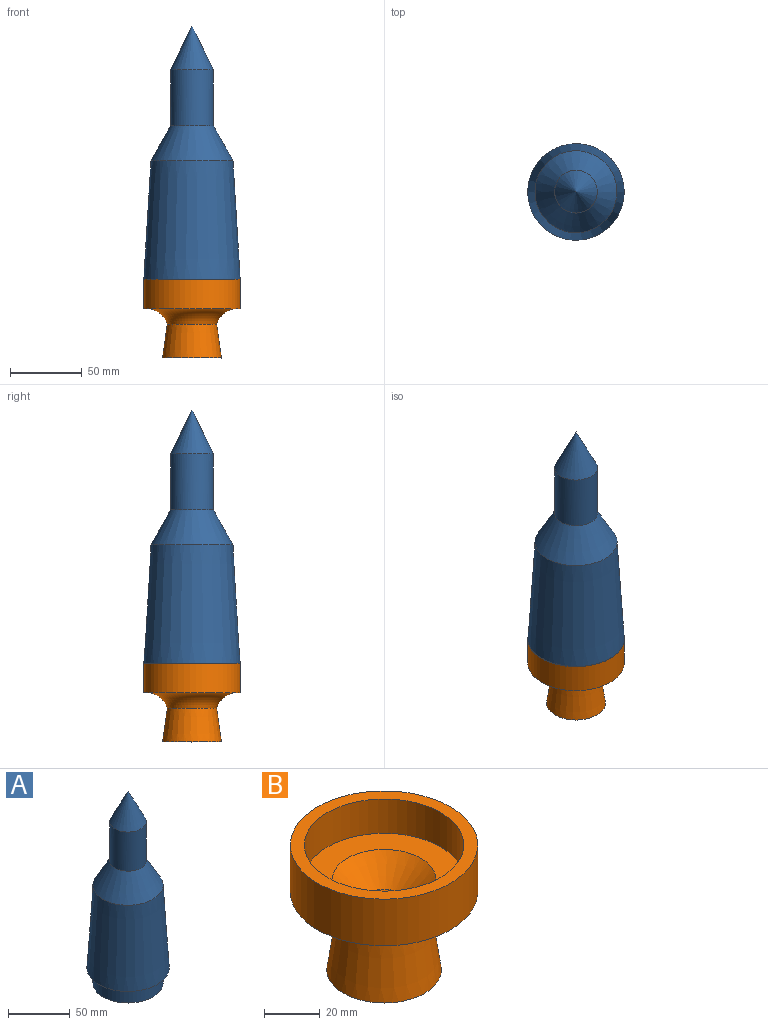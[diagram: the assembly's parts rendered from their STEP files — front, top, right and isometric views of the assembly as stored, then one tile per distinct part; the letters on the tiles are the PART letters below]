
ASSEMBLY  parts=2 mates=1
PART A: 13 faces, bbox 67x67x191 mm
  f0: cylinder r=28.5mm len=57mm, axis (0,0,1), area 2686.1mm2, adj f1,f12
  f1: plane 57x57mm, normal (0,0,-1), area 1476.5mm2, adj f0,f2
  f2: cone r=18.5mm half-angle=14.6deg, axis (0,0,1), area 3375.5mm2, adj f1,f3
  f3: cylinder r=24.75mm len=53.85mm, axis (0,0,1), area 8372.8mm2, adj f2,f4
  f4: revolved ~49.49x49.49mm, area 3906.6mm2, adj f3,f5
  f5: cone r=10.07mm half-angle=36.8deg, axis (0,0,1), area 430.9mm2, adj f4,f6
  f6: cylinder r=10.07mm len=46.25mm, axis (0,0,1), area 2925.6mm2, adj f5,f7
  f7: plane 20.13x20.13mm, normal (0,0,-1), area 318.4mm2, adj f6
  f8: cone r=14.84mm half-angle=26deg, axis (0,0,-1), area 1578.3mm2, adj f9
  f9: cylinder r=14.84mm len=38.88mm, axis (0,0,1), area 3626.4mm2, adj f8,f10
  f10: cone r=28.5mm half-angle=29.3deg, axis (0,0,-1), area 3800.7mm2, adj f9,f11
  f11: cone r=33.5mm half-angle=3.5deg, axis (0,0,-1), area 16063.3mm2, adj f10,f12
  f12: plane 67x67mm, normal (0,0,-1), area 973.9mm2, adj f0,f11
PART B: 10 faces, bbox 92.1x92.1x54.6 mm
  f0: cone r=6.8mm half-angle=15deg, axis (0,0,-1), area 1817.4mm2, adj f1,f9
  f1: torus R=9.7mm, axis (0,0,1), area 144.1mm2, adj f0,f2
  f2: cone r=18.5mm half-angle=47.9deg, axis (0,0,1), area 1199.5mm2, adj f1,f3
  f3: plane 57x57mm, normal (0,0,1), area 1476.5mm2, adj f2,f4
  f4: cylinder r=28.5mm len=57mm, axis (0,0,1), area 2686.1mm2, adj f3,f5
  f5: plane 67x67mm, normal (0,0,1), area 973.9mm2, adj f4,f6
  f6: cylinder r=33.5mm len=67mm, axis (0,0,1), area 4294.6mm2, adj f5,f7
  f7: torus R=31.74mm, axis (0,0,1), area 3200.8mm2, adj f6,f8
  f8: cone r=20.47mm half-angle=8deg, axis (0,0,-1), area 2813.2mm2, adj f7,f9
  f9: plane 40.94x40.94mm, normal (0,0,-1), area 700.8mm2, adj f0,f8
PLACE A t=(145.3,-170.79,9.74)mm
PLACE B rot(axis=(0,0,1),149.2deg) t=(145.3,-170.79,44.45)mm
MATE cylindrical A.f0 <-> B.f0  axis (0,0,-1) through (145.3,-170.79,89.62)mm
